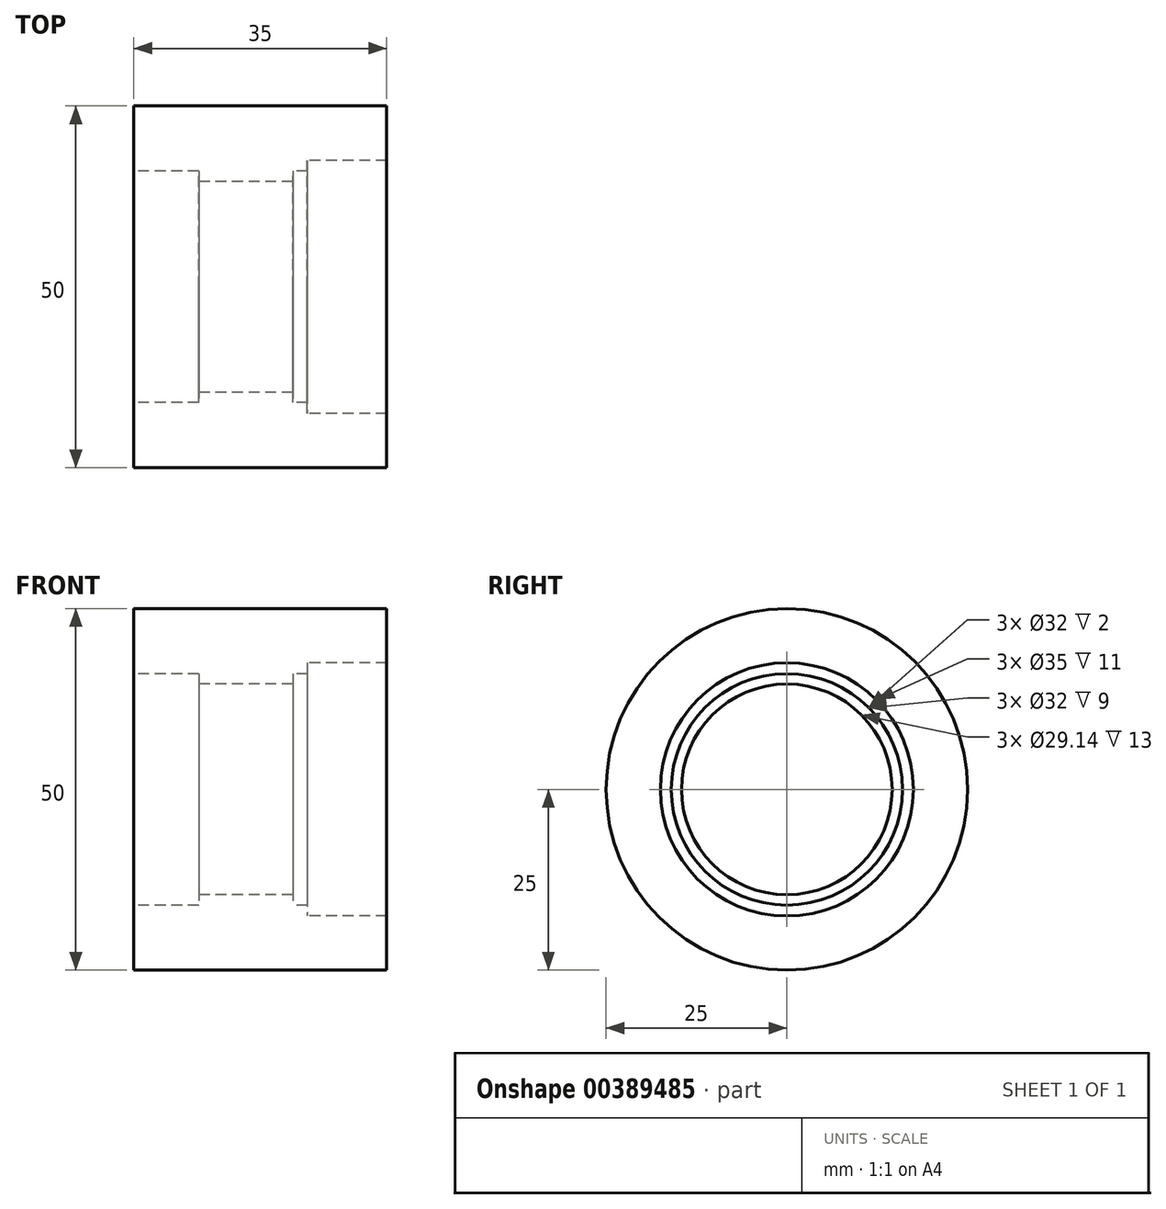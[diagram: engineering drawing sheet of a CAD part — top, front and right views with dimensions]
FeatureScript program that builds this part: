
annotation { "Feature Type Name" : "Feature", "Feature Type Description" : "" }
export const myFeature = defineFeature(function(context is Context, id is Id, definition is map)
    precondition{}
    {
        {
            var Q0;
            Q0=qCreatedBy(makeId("Front.planeOp"),FACE);
            var sketch = newSketch(context, id + "F0", { "sketchPlane" : qUnion([Q0])});
            skLineSegment(sketch, "E0", {"start": v(-22, 25) * mm, "end": v(-22, 16) * mm});
            skLineSegment(sketch, "E1", {"start": v(13, 17.5) * mm, "end": v(13, 25) * mm});
            skLineSegment(sketch, "E2", {"start": v(13, 17.5) * mm, "end": v(2, 17.5) * mm, "construction": true});
            skLineSegment(sketch, "E3", {"start": v(2, 17.5) * mm, "end": v(13, 17.5) * mm});
            skLineSegment(sketch, "E4", {"start": v(0, 0) * mm, "end": v(35.37, 0) * mm, "construction": true});
            skLineSegment(sketch, "E5", {"start": v(-22, 16) * mm, "end": v(-13, 16) * mm});
            skLineSegment(sketch, "E6", {"start": v(-13, 16) * mm, "end": v(-13, 14.57) * mm});
            skLineSegment(sketch, "E7", {"start": v(2, 17.5) * mm, "end": v(2, 16) * mm});
            skLineSegment(sketch, "E8", {"start": v(2, 16) * mm, "end": v(0, 16) * mm});
            skLineSegment(sketch, "E9", {"start": v(0, 16) * mm, "end": v(0, 14.57) * mm});
            skLineSegment(sketch, "E10", {"start": v(0, 14.57) * mm, "end": v(-13, 14.57) * mm});
            skLineSegment(sketch, "E11", {"start": v(-22, 25) * mm, "end": v(13, 25) * mm});
            skSolve(sketch);
        }
        {
            var Q0;
            Q0=makeQuery(id+"F0.imprint","IMPRINT",FACE,{"disambiguationData":[TD([[makeQuery(id+"F0.imprint","IMPRINT",EDGE,{"derivedFrom":sQuery(id+"F0.wireOp",EDGE,"E0")}),1.0]])]});
            var Q1;
            Q1=sQuery(id+"F0.wireOp",EDGE,"E4");
            revolve(context, id + "F1", {"entities" : qUnion([Q0]), "axis" : qUnion([Q1]), "revolveType" : RevolveType.FULL});
        }
    });
